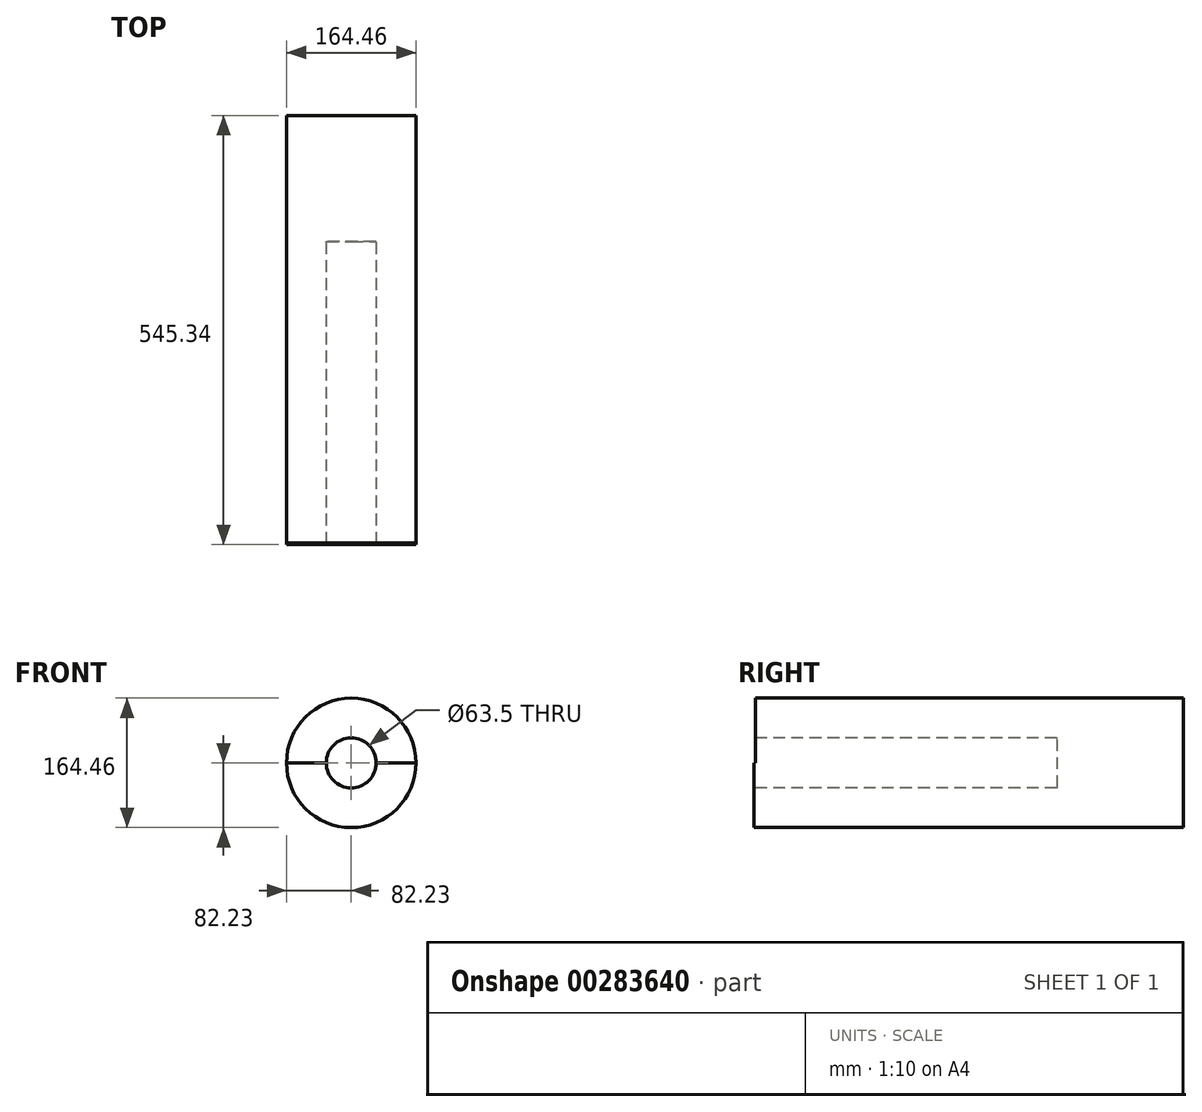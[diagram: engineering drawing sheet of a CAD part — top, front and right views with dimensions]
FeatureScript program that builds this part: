
annotation { "Feature Type Name" : "Feature", "Feature Type Description" : "" }
export const myFeature = defineFeature(function(context is Context, id is Id, definition is map)
    precondition{}
    {
        {
            var Q0;
            Q0=qCreatedBy(makeId("Front.planeOp"),FACE);
            var sketch = newSketch(context, id + "F0", { "sketchPlane" : qUnion([Q0])});
            skCircle(sketch, "E0", {"center": v(0, 0) * mm, "radius": 82.23 * mm});
            skSolve(sketch);
        }
        {
            var Q0;
            Q0 = qSketchRegion(id + "F0", true);
            extrude(context, id + "F1", {"entities" : qUnion([Q0]), "depth" : 545.34 * mm});
        }
        {
            var Q0;
            Q0=makeQuery(id+"F1.opExtrude","CAP_FACE",FACE,{"disambiguationData":[OSD([sQuery(id+"F0.wireOp",EDGE,"E0")])],"isStart":false});
            var sketch = newSketch(context, id + "F2", { "sketchPlane" : qUnion([Q0])});
            skCircle(sketch, "E1", {"center": v(0, 0) * mm, "radius": 31.75 * mm});
            skSolve(sketch);
        }
        {
            var Q0;
            Q0 = qSketchRegion(id + "F2", true);
            extrude(context, id + "F3", {"entities" : qUnion([Q0]), "operationType" : NewBodyOperationType.REMOVE, "oppositeDirection" : true, "depth" : 385.32 * mm});
        }
        {
            var Q0;
            Q0=makeQuery(id+"F3.boolean.opBoolean","COPY",EDGE,{"derivedFrom":makeQuery(id+"F3.opExtrude","CAP_EDGE",EDGE,{"disambiguationData":[OSD([sQuery(id+"F2.wireOp",EDGE,"E1")])],"isStart":false})});
            fillet(context, id + "F4", {"entities" : qUnion([Q0]), "radius" : 0.89 * mm, "tangentPropagation" : true, "allowEdgeOverflow" : false});
        }
        {
            var Q0;
            Q0=makeQuery(id+"F1.opExtrude","CAP_FACE",FACE,{"disambiguationData":[OSD([sQuery(id+"F0.wireOp",EDGE,"E0")])],"isStart":false});
            var sketch = newSketch(context, id + "F5", { "sketchPlane" : qUnion([Q0])});
            skLineSegment(sketch, "E2", {"start": v(-90.93, 0) * mm, "end": v(99.85, 0) * mm});
            skLineSegment(sketch, "E3", {"start": v(99.85, 0) * mm, "end": v(85.32, 66.09) * mm});
            skLineSegment(sketch, "E4", {"start": v(85.32, 66.09) * mm, "end": v(21.1, 103.59) * mm});
            skLineSegment(sketch, "E5", {"start": v(21.1, 103.59) * mm, "end": v(-59.53, 95.15) * mm});
            skLineSegment(sketch, "E6", {"start": v(-59.53, 95.15) * mm, "end": v(-94.68, 75) * mm});
            skLineSegment(sketch, "E7", {"start": v(-94.68, 75) * mm, "end": v(-90.93, 0) * mm});
            skSolve(sketch);
        }
        {
            var Q0;
            Q0 = qSketchRegion(id + "F5", true);
            extrude(context, id + "F6", {"entities" : qUnion([Q0]), "operationType" : NewBodyOperationType.REMOVE, "oppositeDirection" : true, "depth" : 2 * mm});
        }
    });
